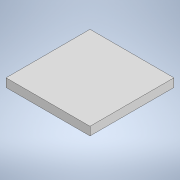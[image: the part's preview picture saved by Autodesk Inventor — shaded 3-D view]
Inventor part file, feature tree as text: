
AUTODESK INVENTOR PART (.ipt)
format: ipt  version: 2020 (Build 240168000, 168)  size: 210,432 bytes
history: native  units: in
note: dims shown in document units (in); Inventor stores cm internally (conversion verified against a paired STEP export)
features: other x3, fillet x2, sketch x2, boolean_combine x1
ambient origin geometry x8: Origin, YZ Plane, XZ Plane, XY Plane, X Axis, Y Axis, Z Axis, Center Point
bodies: Solid1 (feature_tree), Solid2 (feature_tree)
feature tree (8):
  other  "Alliance Marker - Red.iam"
  other  "Alliance Marker - Red.ipt:1"
  other  "Mount Male.ipt:1"
  boolean_combine  "Combine1"
  fillet  "Fillet1"  Radius=0.3937in
  fillet  "Fillet2"  Radius=0.4in
  sketch  "Sketch5"
  sketch  "Sketch5_1"  dims[d2=0.1in]
